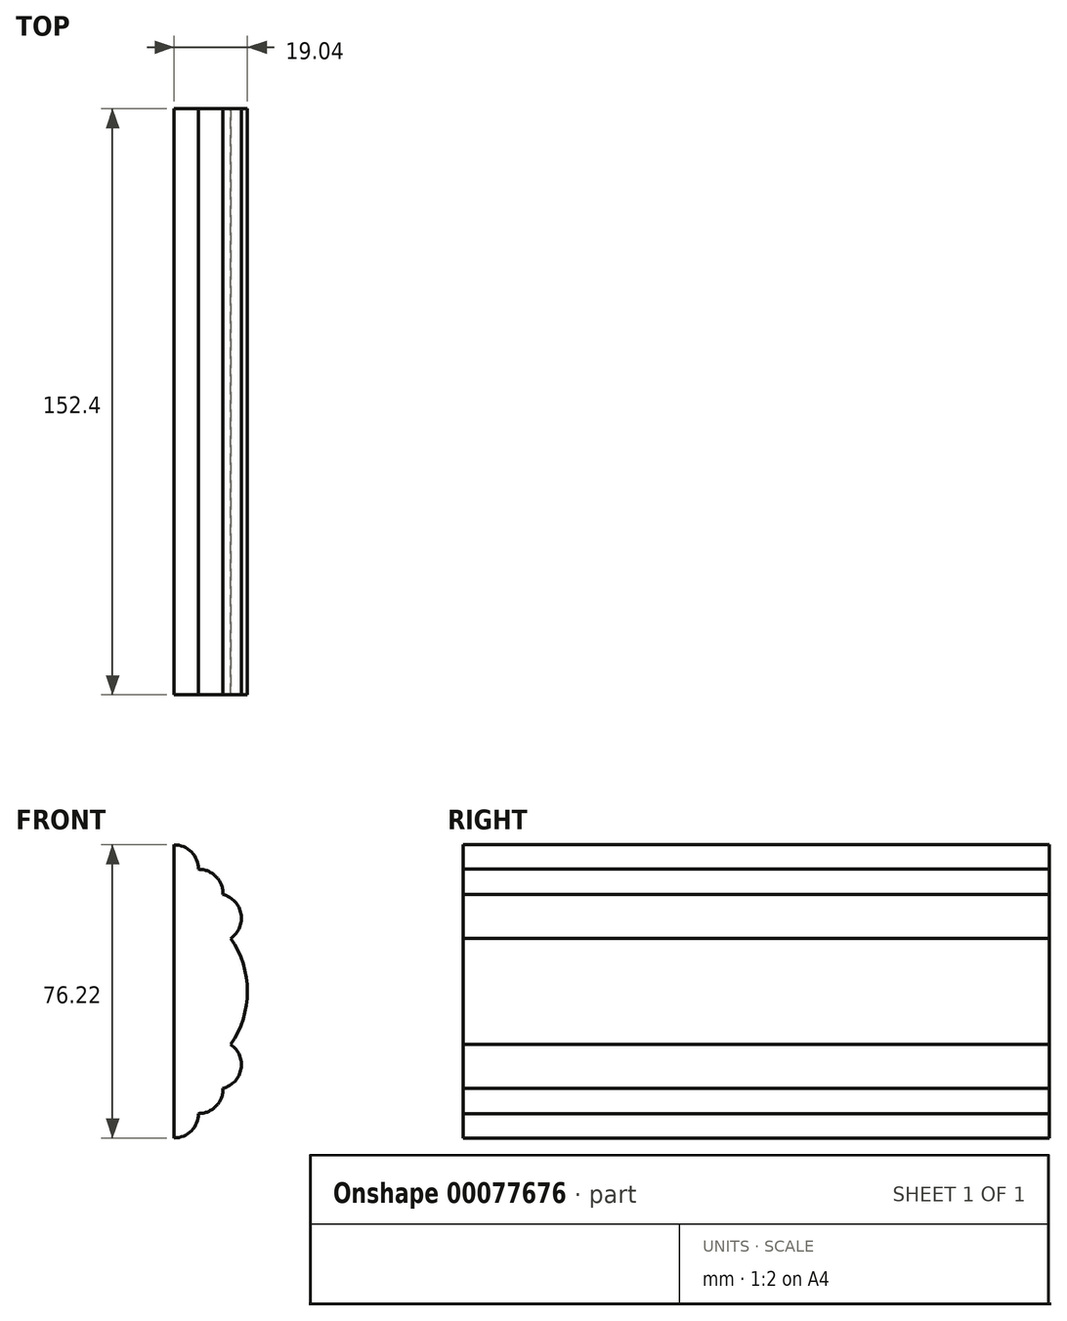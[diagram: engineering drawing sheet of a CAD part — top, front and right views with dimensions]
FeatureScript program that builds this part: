
annotation { "Feature Type Name" : "Feature", "Feature Type Description" : "" }
export const myFeature = defineFeature(function(context is Context, id is Id, definition is map)
    precondition{}
    {
        {
            var Q0;
            Q0=qCreatedBy(makeId("Front.planeOp"),FACE);
            var sketch = newSketch(context, id + "F0", { "sketchPlane" : qUnion([Q0])});
            skLineSegment(sketch, "E0", {"start": v(-9.53, 38.1) * mm, "end": v(-9.53, -38.1) * mm});
            skArc(sketch, "E1", {"start": v(-3.17, 31.76) * mm, "mid": v(-5.03, 36.25) * mm, "end": v(-9.53, 38.1) * mm});
            skArc(sketch, "E2", {"start": v(3.17, 25.2) * mm, "mid": v(1.39, 29.82) * mm, "end": v(-3.17, 31.76) * mm});
            skArc(sketch, "E3", {"start": v(7.94, 19.05) * mm, "mid": v(6.6, 22.94) * mm, "end": v(3.17, 25.2) * mm});
            skArc(sketch, "E4", {"start": v(5.18, 13.82) * mm, "mid": v(7.2, 16.1) * mm, "end": v(7.94, 19.05) * mm});
            skArc(sketch, "E5", {"start": v(-3.17, -31.76) * mm, "mid": v(1.39, -29.82) * mm, "end": v(3.17, -25.2) * mm});
            skArc(sketch, "E6", {"start": v(-9.53, -38.1) * mm, "mid": v(-5.03, -36.25) * mm, "end": v(-3.17, -31.76) * mm});
            skArc(sketch, "E7", {"start": v(5.18, -13.82) * mm, "mid": v(9.51, 0) * mm, "end": v(5.18, 13.82) * mm});
            skArc(sketch, "E8", {"start": v(3.17, -25.2) * mm, "mid": v(6.6, -22.94) * mm, "end": v(7.94, -19.05) * mm});
            skArc(sketch, "E9", {"start": v(7.94, -19.05) * mm, "mid": v(7.2, -16.1) * mm, "end": v(5.18, -13.82) * mm});
            skSolve(sketch);
        }
        {
            var Q0;
            {var subQ0=sQuery(id+"F0.wireOp",EDGE,"E0");Q0=makeQuery(id+"F0.imprint","IMPRINT",FACE,{"disambiguationData":[TD([[makeQuery(id+"F0.imprint","IMPRINT",EDGE,{"derivedFrom":subQ0}),1.0]])]});}
            extrude(context, id + "F1", {"entities" : qUnion([Q0]), "depth" : 152.4 * mm});
        }
    });
